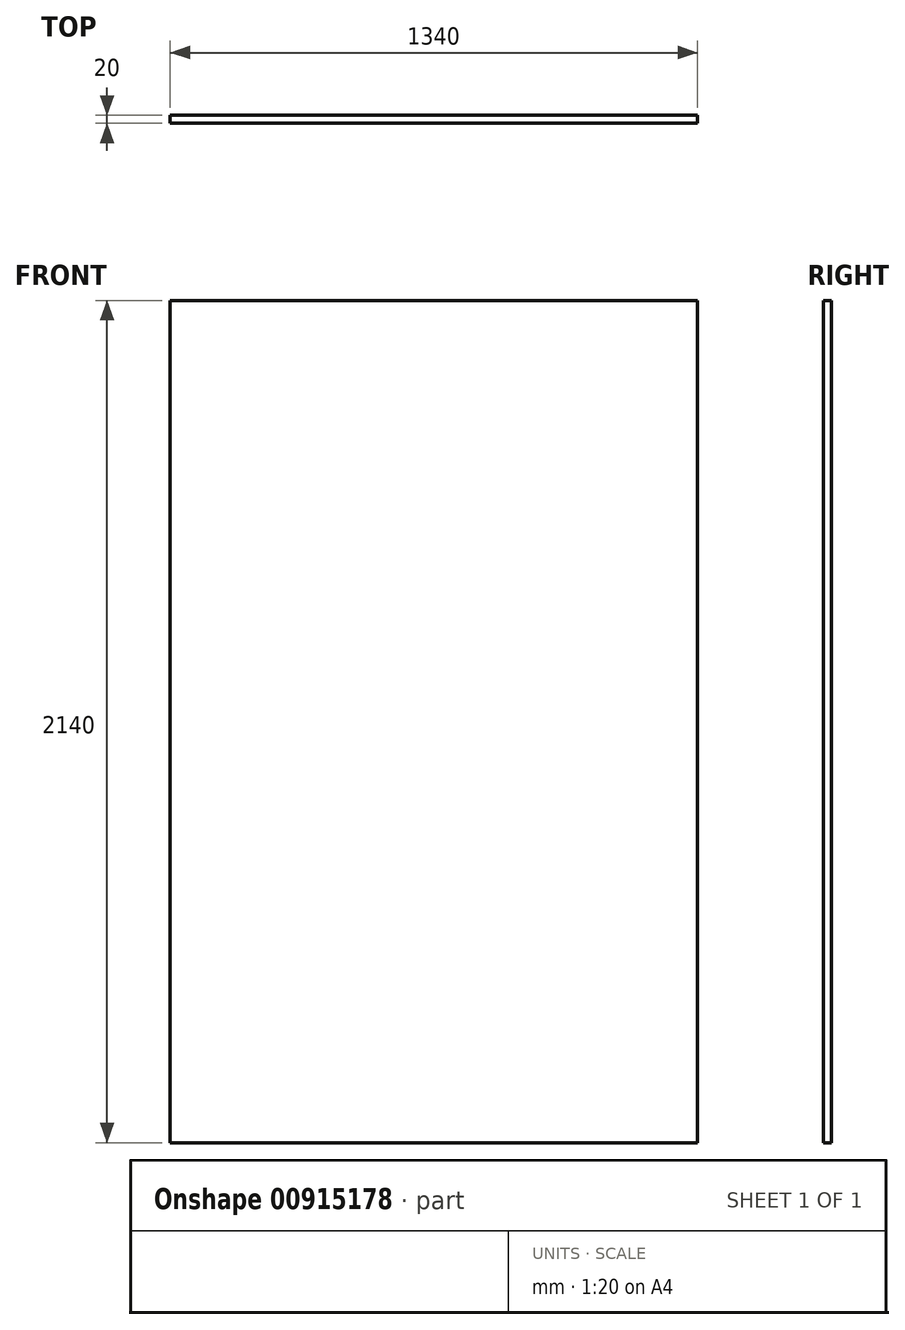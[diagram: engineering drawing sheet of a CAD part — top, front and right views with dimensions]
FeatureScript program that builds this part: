
annotation { "Feature Type Name" : "Feature", "Feature Type Description" : "" }
export const myFeature = defineFeature(function(context is Context, id is Id, definition is map)
    precondition{}
    {
        {
            var Q0;
            Q0=qCreatedBy(makeId("Front.planeOp"),FACE);
            var sketch = newSketch(context, id + "F0", { "sketchPlane" : qUnion([Q0])});
            skLineSegment(sketch, "E0", {"start": v(-70.4, 0) * mm, "end": v(1269.6, 0) * mm});
            skLineSegment(sketch, "E1", {"start": v(1269.6, 0) * mm, "end": v(1269.6, 2140) * mm});
            skLineSegment(sketch, "E2", {"start": v(1269.6, 2140) * mm, "end": v(-70.4, 2140) * mm});
            skLineSegment(sketch, "E3", {"start": v(-70.4, 2140) * mm, "end": v(-70.4, 0) * mm});
            skSolve(sketch);
        }
        {
            var Q0;
            Q0 = qSketchRegion(id + "F0", true);
            extrude(context, id + "F1", {"entities" : qUnion([Q0]), "depth" : 20 * mm, "offsetDistance" : 25 * mm});
        }
    });
